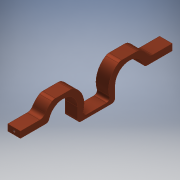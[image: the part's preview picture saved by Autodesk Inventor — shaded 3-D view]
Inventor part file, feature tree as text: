
AUTODESK INVENTOR PART (.ipt)
format: ipt  version: 2018 (Build 220112000, 112)  size: 170,496 bytes
history: native  units: mm
features: sketch x2, extrude x1, hole x1, mirror x1, fillet x1, projected_geometry x1
ambient origin geometry x8: Origin, YZ Plane, XZ Plane, XY Plane, X Axis, Y Axis, Z Axis, Center Point
bodies: Solid1 (feature_tree)
feature tree (7):
  extrude  "Extrusion1"  Depth=9.25mm
  hole  "Hole1"  [1 undecoded]
  mirror  "Mirror1"
  fillet  "Fillet3"  Radius=4.0mm
  sketch  "Sketch1"  dims[d1=9.25mm d3=42.0mm]
  sketch  "Sketch2"  dims[d4=96.0mm d5=4.0mm d8=4.0mm d9=8.0mm d10=0.0mm d11=0.3mm d13=10.1mm d14=9.15mm d15=21.0mm d19=1.567mm d20=4.0mm d21=4.0mm d22=2.0mm d23=90.0deg d24=6.3mm d25=20.594885mm d26=2.0mm d30=2.0mm d31=13.083569mm d32=4.0mm d33=2.0mm]
  projected_geometry  "Projected Loop1"
note: 1 required parameter value undecoded (feature->parameter linkage not recoverable at this tier; creation-order binding heuristic only, values carry confidence <= 0.55)
